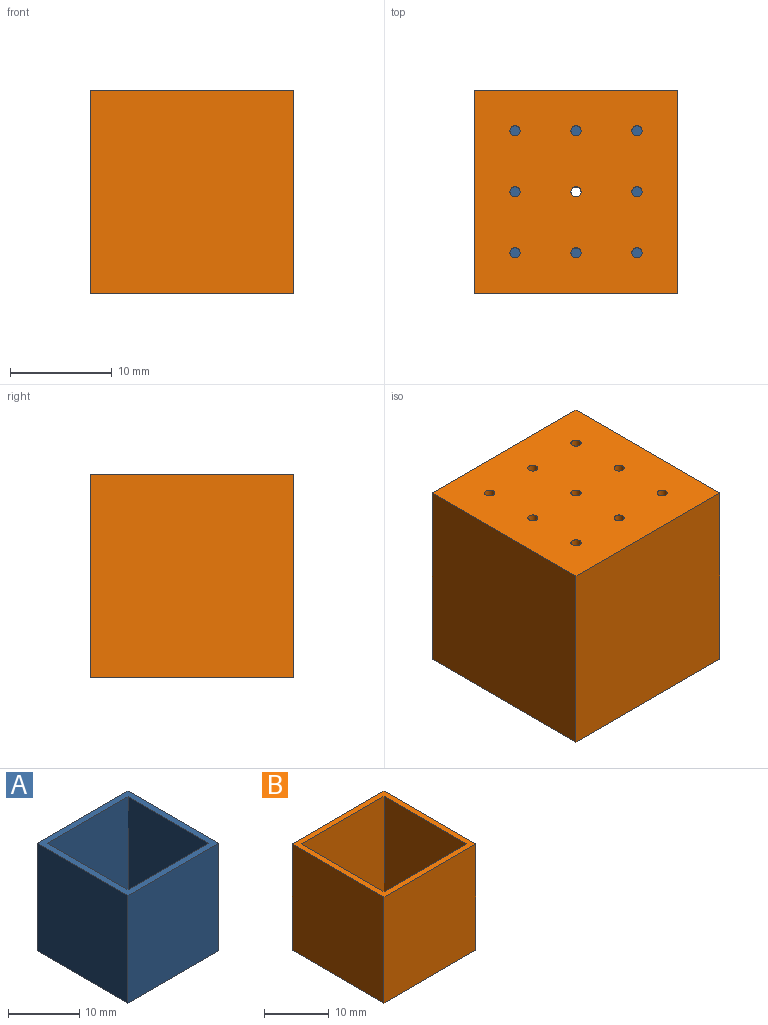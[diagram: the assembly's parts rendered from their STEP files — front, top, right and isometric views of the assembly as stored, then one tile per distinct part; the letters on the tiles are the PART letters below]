
ASSEMBLY  parts=2 mates=1
PART A: 20 faces, bbox 18x18x18.5 mm
  f0: plane 18.5x18mm, normal (-1,0,0), area 333mm2, adj f1,f3,f4,f5
  f1: plane 18.5x18mm, normal (0,-1,0), area 333mm2, adj f0,f2,f4,f5
  f2: plane 18.5x18mm, normal (1,0,0), area 333mm2, adj f1,f3,f4,f5
  f3: plane 18.5x18mm, normal (0,1,0), area 333mm2, adj f0,f2,f4,f5
  f4: plane 18x18mm, normal (0,0,1), area 68mm2, adj f0,f1,f2,f3,f6,f7,f8,f9
  f5: plane 18x18mm, normal (0,0,-1), area 316.9mm2, adj f0,f1,f2,f3,f11,f12,f13,f14
  f6: plane 17.5x16mm, normal (1,0,0), area 280mm2, adj f4,f7,f9,f10
  f7: plane 17.5x16mm, normal (0,1,0), area 280mm2, adj f4,f6,f8,f10
  f8: plane 17.5x16mm, normal (-1,0,0), area 280mm2, adj f4,f7,f9,f10
  f9: plane 17.5x16mm, normal (0,-1,0), area 280mm2, adj f4,f6,f8,f10
  f10: plane 16x16mm, normal (0,0,1), area 248.9mm2, adj f6,f7,f8,f9,f11,f12,f13,f14
  f11: cylinder r=0.5mm len=1mm, axis (0,0,-1), area 3.1mm2, adj f5,f10
  f12: cylinder r=0.5mm len=1mm, axis (0,0,-1), area 3.1mm2, adj f5,f10
  f13: cylinder r=0.5mm len=1mm, axis (0,0,-1), area 3.1mm2, adj f5,f10
  f14: cylinder r=0.5mm len=1mm, axis (0,0,-1), area 3.1mm2, adj f5,f10
  f15: cylinder r=0.5mm len=1mm, axis (0,0,-1), area 3.1mm2, adj f5,f10
  f16: cylinder r=0.5mm len=1mm, axis (0,0,-1), area 3.1mm2, adj f5,f10
  f17: cylinder r=0.5mm len=1mm, axis (0,0,-1), area 3.1mm2, adj f5,f10
  f18: cylinder r=0.5mm len=1mm, axis (0,0,-1), area 3.1mm2, adj f5,f10
  f19: cylinder r=0.5mm len=1mm, axis (0,0,-1), area 3.1mm2, adj f5,f10
PART B: 20 faces, bbox 20x20x20 mm
  f0: plane 20x20mm, normal (-1,0,0), area 400mm2, adj f1,f3,f4,f5
  f1: plane 20x20mm, normal (0,-1,0), area 400mm2, adj f0,f2,f4,f5
  f2: plane 20x20mm, normal (1,0,0), area 400mm2, adj f1,f3,f4,f5
  f3: plane 20x20mm, normal (0,1,0), area 400mm2, adj f0,f2,f4,f5
  f4: plane 20x20mm, normal (0,0,1), area 76mm2, adj f0,f1,f2,f3,f6,f7,f8,f9
  f5: plane 20x20mm, normal (0,0,-1), area 392.9mm2, adj f0,f1,f2,f3,f11,f12,f13,f14
  f6: plane 19x18mm, normal (1,0,0), area 342mm2, adj f4,f7,f9,f10
  f7: plane 19x18mm, normal (0,1,0), area 342mm2, adj f4,f6,f8,f10
  f8: plane 19x18mm, normal (-1,0,0), area 342mm2, adj f4,f7,f9,f10
  f9: plane 19x18mm, normal (0,-1,0), area 342mm2, adj f4,f6,f8,f10
  f10: plane 18x18mm, normal (0,0,1), area 316.9mm2, adj f6,f7,f8,f9,f11,f12,f13,f14
  f11: cylinder r=0.5mm len=1mm, axis (0,0,-1), area 3.1mm2, adj f5,f10
  f12: cylinder r=0.5mm len=1mm, axis (0,0,-1), area 3.1mm2, adj f5,f10
  f13: cylinder r=0.5mm len=1mm, axis (0,0,-1), area 3.1mm2, adj f5,f10
  f14: cylinder r=0.5mm len=1mm, axis (0,0,-1), area 3.1mm2, adj f5,f10
  f15: cylinder r=0.5mm len=1mm, axis (0,0,-1), area 3.1mm2, adj f5,f10
  f16: cylinder r=0.5mm len=1mm, axis (0,0,-1), area 3.1mm2, adj f5,f10
  f17: cylinder r=0.5mm len=1mm, axis (0,0,-1), area 3.1mm2, adj f5,f10
  f18: cylinder r=0.5mm len=1mm, axis (0,0,-1), area 3.1mm2, adj f5,f10
  f19: cylinder r=0.5mm len=1mm, axis (0,0,-1), area 3.1mm2, adj f5,f10
PLACE A rot(axis=(0.71,0.4,-0.58),0deg) t=(-1.45,-1.63,-5.38)mm
PLACE B rot(axis=(0,-1,0),180deg) t=(14.5,-2.63,14.12)mm
MATE fastened B.f10 <-> A.f4  axis (0,0,1) through (-2.98,-10.19,13.12)mm
